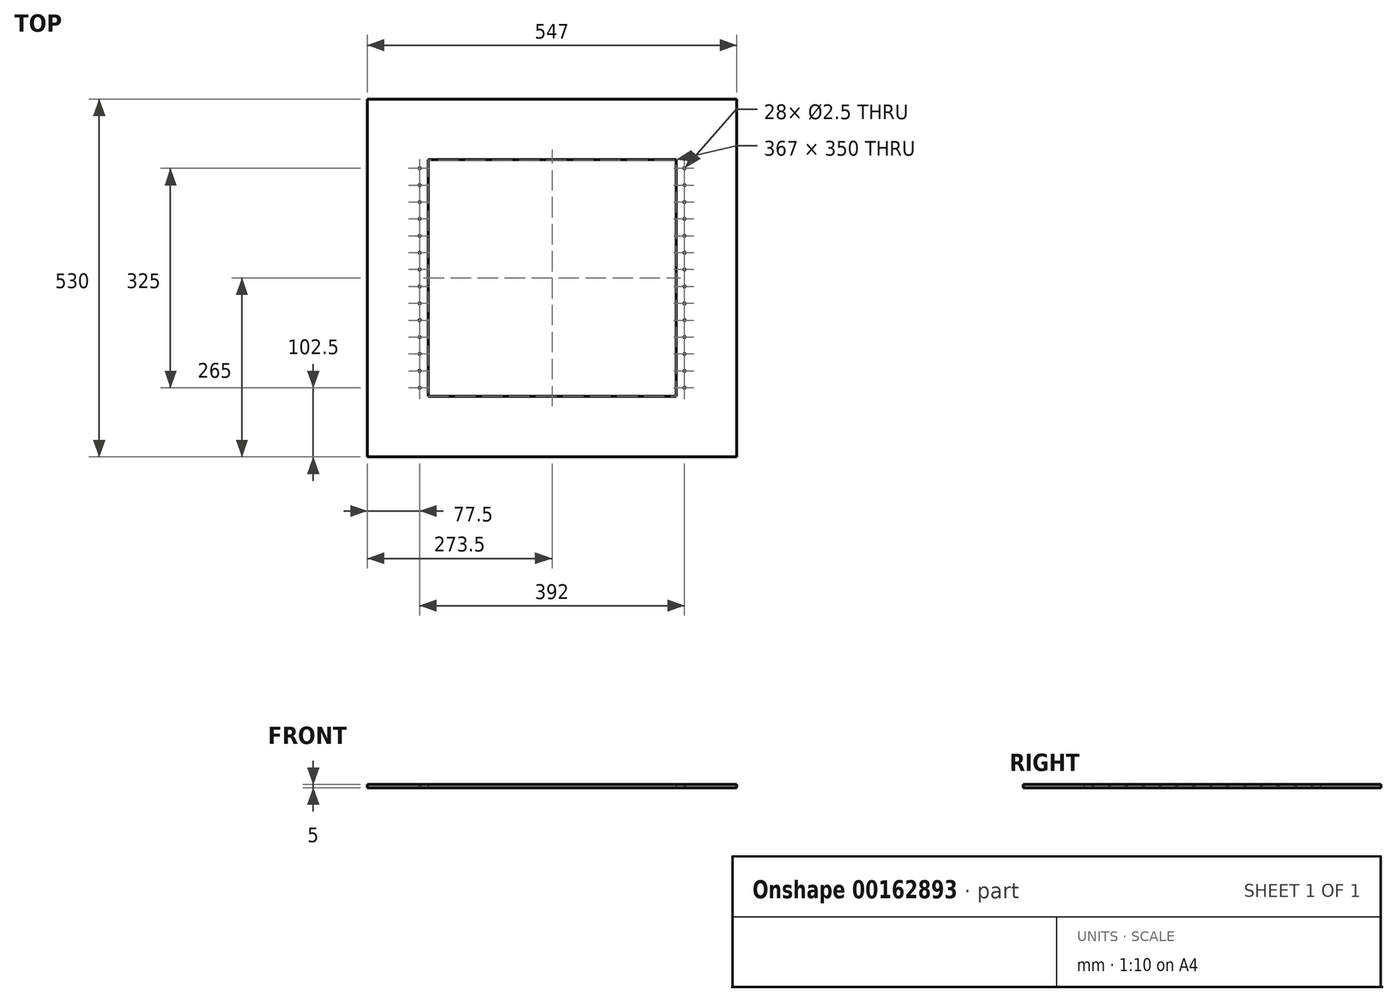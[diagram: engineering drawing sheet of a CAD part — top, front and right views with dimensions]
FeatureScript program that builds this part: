
annotation { "Feature Type Name" : "Feature", "Feature Type Description" : "" }
export const myFeature = defineFeature(function(context is Context, id is Id, definition is map)
    precondition{}
    {
        {
            var Q0;
            Q0=qCreatedBy(makeId("Top.planeOp"),FACE);
            var sketch = newSketch(context, id + "F0", { "sketchPlane" : qUnion([Q0])});
            skLineSegment(sketch, "E0.bottom", {"start": v(183.5, -175) * mm, "end": v(-183.5, -175) * mm});
            skLineSegment(sketch, "E0.top", {"start": v(183.5, 175) * mm, "end": v(-183.5, 175) * mm});
            skLineSegment(sketch, "E0.left", {"start": v(183.5, -175) * mm, "end": v(183.5, 175) * mm});
            skLineSegment(sketch, "E0.right", {"start": v(-183.5, -175) * mm, "end": v(-183.5, 175) * mm});
            skPoint(sketch, "E0.middle", {"position": v(0, 0) * mm});
            skLineSegment(sketch, "E1.bottom", {"start": v(273.5, -265) * mm, "end": v(-273.5, -265) * mm});
            skLineSegment(sketch, "E1.top", {"start": v(273.5, 265) * mm, "end": v(-273.5, 265) * mm});
            skLineSegment(sketch, "E1.left", {"start": v(273.5, -265) * mm, "end": v(273.5, 265) * mm});
            skLineSegment(sketch, "E1.right", {"start": v(-273.5, -265) * mm, "end": v(-273.5, 265) * mm});
            skLineSegment(sketch, "E2", {"start": v(-196, 150) * mm, "end": v(-196, -150) * mm, "construction": true});
            skPoint(sketch, "E3", {"position": v(-196, 0) * mm});
            skPoint(sketch, "E4", {"position": v(-196, -162.5) * mm});
            skPoint(sketch, "E5.0.1.0", {"position": v(-196, -137.5) * mm});
            skPoint(sketch, "E5.0.2.0", {"position": v(-196, -112.5) * mm});
            skPoint(sketch, "E5.0.3.0", {"position": v(-196, -87.5) * mm});
            skPoint(sketch, "E5.0.4.0", {"position": v(-196, -62.5) * mm});
            skPoint(sketch, "E5.0.5.0", {"position": v(-196, -37.5) * mm});
            skPoint(sketch, "E5.0.6.0", {"position": v(-196, -12.5) * mm});
            skPoint(sketch, "E5.0.7.0", {"position": v(-196, 12.5) * mm});
            skPoint(sketch, "E5.0.8.0", {"position": v(-196, 37.5) * mm});
            skPoint(sketch, "E5.0.9.0", {"position": v(-196, 62.5) * mm});
            skPoint(sketch, "E5.0.10.0", {"position": v(-196, 87.5) * mm});
            skPoint(sketch, "E5.0.11.0", {"position": v(-196, 112.5) * mm});
            skLineSegment(sketch, "E5.direction1", {"start": v(-196, -162.5) * mm, "end": v(-135, -162.5) * mm, "construction": true});
            skLineSegment(sketch, "E5.direction2", {"start": v(-196, -162.5) * mm, "end": v(-196, -137.5) * mm, "construction": true});
            skPoint(sketch, "E6.MirrorP", {"position": v(196, 112.5) * mm});
            skPoint(sketch, "E7.MirrorP", {"position": v(196, 87.5) * mm});
            skPoint(sketch, "E8.MirrorP", {"position": v(196, 62.5) * mm});
            skPoint(sketch, "E9.MirrorP", {"position": v(196, 37.5) * mm});
            skPoint(sketch, "E10.MirrorP", {"position": v(196, 12.5) * mm});
            skPoint(sketch, "E11.MirrorP", {"position": v(196, -12.5) * mm});
            skPoint(sketch, "E12.MirrorP", {"position": v(196, -37.5) * mm});
            skPoint(sketch, "E13.MirrorP", {"position": v(196, -62.5) * mm});
            skPoint(sketch, "E14.MirrorP", {"position": v(196, -87.5) * mm});
            skPoint(sketch, "E15.MirrorP", {"position": v(196, -112.5) * mm});
            skPoint(sketch, "E16.MirrorP", {"position": v(196, -137.5) * mm});
            skPoint(sketch, "E17.MirrorP", {"position": v(196, -162.5) * mm});
            skPoint(sketch, "E18.0.0.12", {"position": v(-196, 137.5) * mm});
            skPoint(sketch, "E18.0.0.13", {"position": v(-196, 162.5) * mm});
            skPoint(sketch, "E19.MirrorP", {"position": v(196, 137.5) * mm});
            skPoint(sketch, "E20.MirrorP", {"position": v(196, 162.5) * mm});
            skSolve(sketch);
        }
        {
            var Q0;
            Q0=makeQuery(id+"F0.imprint","IMPRINT",FACE,{"disambiguationData":[TD([[makeQuery(id+"F0.imprint","IMPRINT",EDGE,{"derivedFrom":sQuery(id+"F0.wireOp",EDGE,"E0.bottom")}),1.0]])]});
            extrude(context, id + "F1", {"entities" : qUnion([Q0]), "depth" : 5 * mm, "offsetDistance" : 25 * mm});
        }
        {
            var Q0;
            Q0=sQuery(id+"F0.wireOp",VERTEX,"E5.0.11.0");
            var Q1;
            Q1=sQuery(id+"F0.wireOp",VERTEX,"E5.0.10.0");
            var Q2;
            Q2=sQuery(id+"F0.wireOp",VERTEX,"E5.0.9.0");
            var Q3;
            Q3=sQuery(id+"F0.wireOp",VERTEX,"E5.0.8.0");
            var Q4;
            Q4=sQuery(id+"F0.wireOp",VERTEX,"E5.0.7.0");
            var Q5;
            Q5=sQuery(id+"F0.wireOp",VERTEX,"E5.0.6.0");
            var Q6;
            Q6=sQuery(id+"F0.wireOp",VERTEX,"E5.0.5.0");
            var Q7;
            Q7=sQuery(id+"F0.wireOp",VERTEX,"E5.0.4.0");
            var Q8;
            Q8=sQuery(id+"F0.wireOp",VERTEX,"E5.0.3.0");
            var Q9;
            Q9=sQuery(id+"F0.wireOp",VERTEX,"E5.0.2.0");
            var Q10;
            Q10=sQuery(id+"F0.wireOp",VERTEX,"E5.0.1.0");
            var Q11;
            Q11=sQuery(id+"F0.wireOp",VERTEX,"E4");
            var Q12;
            Q12=sQuery(id+"F0.wireOp",VERTEX,"E17.MirrorP");
            var Q13;
            Q13=sQuery(id+"F0.wireOp",VERTEX,"E16.MirrorP");
            var Q14;
            Q14=sQuery(id+"F0.wireOp",VERTEX,"E15.MirrorP");
            var Q15;
            Q15=sQuery(id+"F0.wireOp",VERTEX,"E14.MirrorP");
            var Q16;
            Q16=sQuery(id+"F0.wireOp",VERTEX,"E13.MirrorP");
            var Q17;
            Q17=sQuery(id+"F0.wireOp",VERTEX,"E12.MirrorP");
            var Q18;
            Q18=sQuery(id+"F0.wireOp",VERTEX,"E11.MirrorP");
            var Q19;
            Q19=sQuery(id+"F0.wireOp",VERTEX,"E10.MirrorP");
            var Q20;
            Q20=sQuery(id+"F0.wireOp",VERTEX,"E9.MirrorP");
            var Q21;
            Q21=sQuery(id+"F0.wireOp",VERTEX,"E8.MirrorP");
            var Q22;
            Q22=sQuery(id+"F0.wireOp",VERTEX,"E7.MirrorP");
            var Q23;
            Q23=sQuery(id+"F0.wireOp",VERTEX,"E6.MirrorP");
            var Q24;
            Q24=sQuery(id+"F0.wireOp",VERTEX,"E18.0.0.12");
            var Q25;
            Q25=sQuery(id+"F0.wireOp",VERTEX,"E18.0.0.13");
            var Q26;
            Q26=sQuery(id+"F0.wireOp",VERTEX,"E19.MirrorP");
            var Q27;
            Q27=sQuery(id+"F0.wireOp",VERTEX,"E20.MirrorP");
            var Q28;
            Q28=makeQuery(id+"F1.opExtrude","SWEPT_BODY",BODY,{"disambiguationData":[OSD([sQuery(id+"F0.wireOp",EDGE,"E0.bottom"),sQuery(id+"F0.wireOp",EDGE,"E0.top"),sQuery(id+"F0.wireOp",EDGE,"E0.left"),sQuery(id+"F0.wireOp",EDGE,"E0.right"),sQuery(id+"F0.wireOp",EDGE,"E1.bottom"),sQuery(id+"F0.wireOp",EDGE,"E1.top"),sQuery(id+"F0.wireOp",EDGE,"E1.left"),sQuery(id+"F0.wireOp",EDGE,"E1.right")])]});
            hole(context, id + "F2", {"style" : HoleStyle.SIMPLE, "endStyle" : HoleEndStyle.THROUGH, "oppositeDirection" : true, "standardTappedOrClearance" : lookupTablePath({ "standard" : "ISO", "engagement" : "75%", "pitch" : "0.5 mm", "size" : "M3", "type" : "Tapped" }), "standardBlindInLast" : lookupTablePath({ "standard" : "ISO", "engagement" : "75%", "pitch" : "0.5 mm", "size" : "M3", "type" : "Tapped" }), "holeDiameter" : 2.5 * mm, "majorDiameter" : 3 * mm, "showTappedDepth" : true, "isTappedThrough" : true, "tappedDepth" : 12 * mm, "tapClearance" : 3, "startFromSketch" : true, "locations" : qUnion([Q0, Q1, Q2, Q3, Q4, Q5, Q6, Q7, Q8, Q9, Q10, Q11, Q12, Q13, Q14, Q15, Q16, Q17, Q18, Q19, Q20, Q21, Q22, Q23, Q24, Q25, Q26, Q27]), "scope" : qUnion([Q28])});
        }
    });
